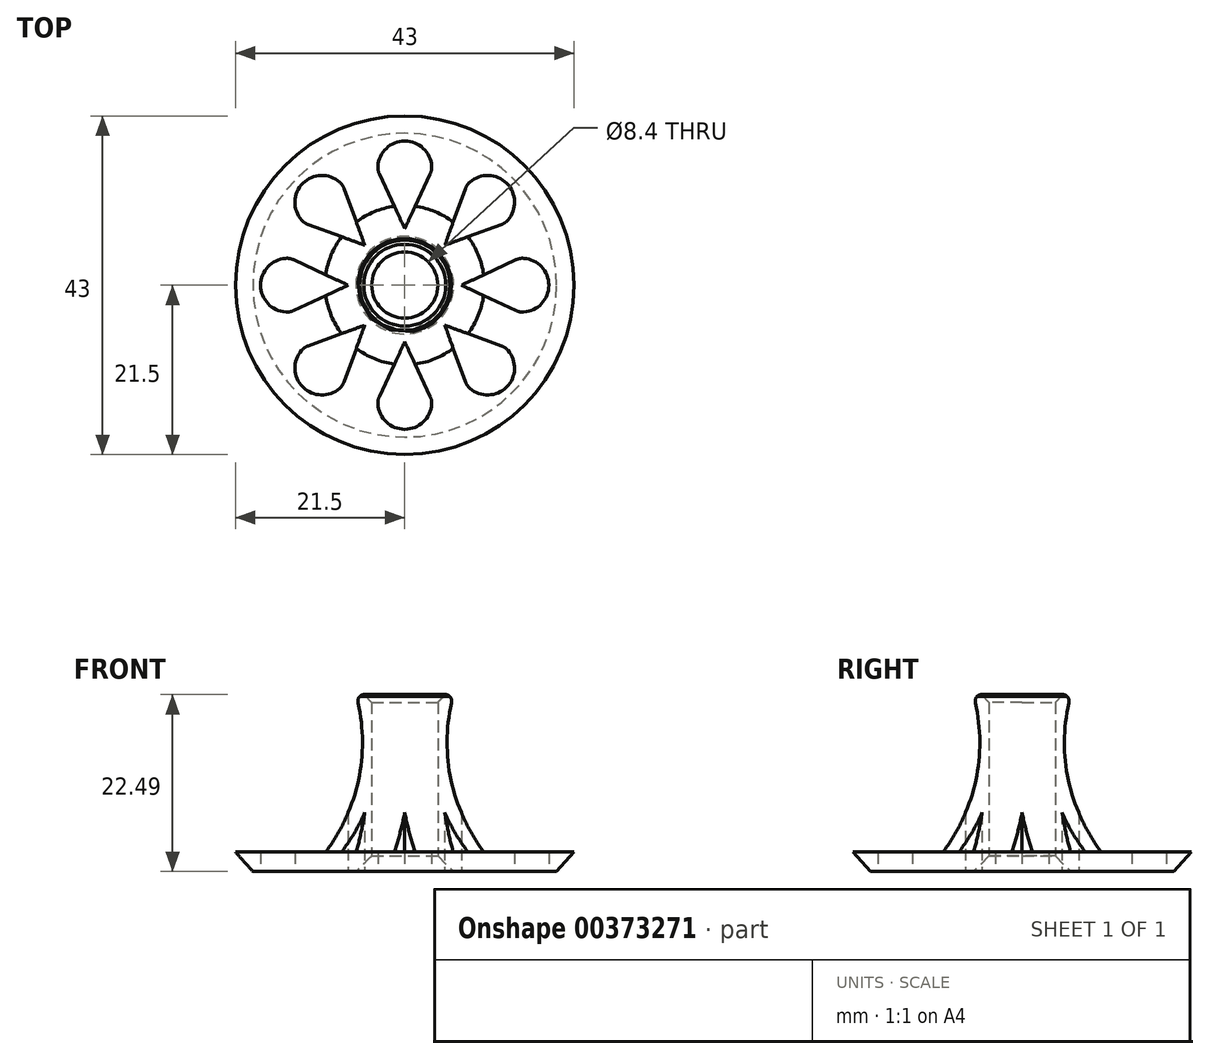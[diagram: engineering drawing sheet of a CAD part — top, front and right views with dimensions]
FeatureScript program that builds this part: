
annotation { "Feature Type Name" : "Feature", "Feature Type Description" : "" }
export const myFeature = defineFeature(function(context is Context, id is Id, definition is map)
    precondition{}
    {
        {
            var Q0;
            Q0=qCreatedBy(makeId("Front.planeOp"),FACE);
            var sketch = newSketch(context, id + "F0", { "sketchPlane" : qUnion([Q0])});
            skLineSegment(sketch, "E0", {"start": v(0, 0) * mm, "end": v(0, 0) * mm});
            skLineSegment(sketch, "E1", {"start": v(4.2, 0) * mm, "end": v(4.2, 22.5) * mm});
            skLineSegment(sketch, "E2", {"start": v(10.1, 2.5) * mm, "end": v(20.5, 2.5) * mm});
            skPoint(sketch, "E3.orphan", {"position": v(4.2, 2.5) * mm});
            skLineSegment(sketch, "E4", {"start": v(0, 0) * mm, "end": v(0, 23.46) * mm, "construction": true});
            skLineSegment(sketch, "E5.trimOffspring", {"start": v(4.2, 0) * mm, "end": v(19.3, 0) * mm});
            skArc(sketch, "E6", {"start": v(6.05, 21.87) * mm, "mid": v(5.86, 11.72) * mm, "end": v(10.1, 2.5) * mm});
            skLineSegment(sketch, "E7", {"start": v(5.53, 22.5) * mm, "end": v(6.05, 21.87) * mm});
            skPoint(sketch, "E8.orphan", {"position": v(7.2, 2.5) * mm});
            skLineSegment(sketch, "E9", {"start": v(4.2, 22.5) * mm, "end": v(5.53, 22.5) * mm});
            skLineSegment(sketch, "E10", {"start": v(20.5, 2.5) * mm, "end": v(21.5, 2.5) * mm});
            skLineSegment(sketch, "E11", {"start": v(19.3, 0) * mm, "end": v(21.5, 2.5) * mm});
            skSolve(sketch);
        }
        {
            var Q0;
            Q0 = qSketchRegion(id + "F0", true);
            var Q1;
            Q1=sQuery(id+"F0.wireOp",EDGE,"E4");
            revolve(context, id + "F1", {"entities" : qUnion([Q0]), "axis" : qUnion([Q1]), "revolveType" : RevolveType.FULL});
        }
        {
            var Q0;
            Q0=makeQuery(id+"F1.opRevolve","SWEPT_EDGE",EDGE,{"disambiguationData":[OSD([sQuery(id+"F0.wireOp",EDGE,"E1"),sQuery(id+"F0.wireOp",EDGE,"E5.trimOffspring")])]});
            chamfer(context, id + "F2", {"entities" : qUnion([Q0]), "width" : 2 * mm, "tangentPropagation" : true});
        }
        {
            var Q0;
            Q0=makeQuery(id+"F1.opRevolve","SWEPT_FACE",FACE,{"disambiguationData":[OSD([sQuery(id+"F0.wireOp",EDGE,"E5.trimOffspring")])]});
            var sketch = newSketch(context, id + "F3", { "sketchPlane" : qUnion([Q0])});
            skCircle(sketch, "E12.0", {"center": v(0, 0) * mm, "radius": 19.3 * mm});
            skCircle(sketch, "E12.1", {"center": v(0, 0) * mm, "radius": 6.2 * mm});
            skLineSegment(sketch, "E13", {"start": v(0, 19.3) * mm, "end": v(0, 0) * mm, "construction": true});
            skLineSegment(sketch, "E14", {"start": v(0, 0) * mm, "end": v(-19.3, 0) * mm, "construction": true});
            skCircle(sketch, "E15", {"center": v(0, 0) * mm, "radius": 14.88 * mm, "construction": true});
            skArc(sketch, "E16", {"start": v(3.41, 15.1) * mm, "mid": v(0, 18.3) * mm, "end": v(-3.41, 15.1) * mm});
            skLineSegment(sketch, "E17", {"start": v(3.23, 14.13) * mm, "end": v(0, 7.19) * mm});
            skLineSegment(sketch, "E18.MirrorCS", {"start": v(-3.23, 14.13) * mm, "end": v(0, 7.19) * mm});
            skPoint(sketch, "E19.visualSharp", {"position": v(-3.4, 14.5) * mm});
            skArc(sketch, "E19.filletArc", {"start": v(-3.41, 15.1) * mm, "mid": v(-3.38, 14.6) * mm, "end": v(-3.23, 14.13) * mm});
            skPoint(sketch, "E20.visualSharp", {"position": v(3.4, 14.5) * mm});
            skArc(sketch, "E20.filletArc", {"start": v(3.23, 14.13) * mm, "mid": v(3.38, 14.6) * mm, "end": v(3.41, 15.1) * mm});
            skArc(sketch, "E21.1.0", {"start": v(-8.27, 13.1) * mm, "mid": v(-12.94, 12.94) * mm, "end": v(-13.1, 8.27) * mm});
            skLineSegment(sketch, "E21.1.1", {"start": v(-12.28, 7.7) * mm, "end": v(-5.08, 5.08) * mm});
            skLineSegment(sketch, "E21.1.2", {"start": v(-7.7, 12.28) * mm, "end": v(-5.08, 5.08) * mm});
            skArc(sketch, "E21.1.3", {"start": v(-7.7, 12.28) * mm, "mid": v(-7.94, 12.72) * mm, "end": v(-8.27, 13.1) * mm});
            skArc(sketch, "E21.1.4", {"start": v(-13.1, 8.27) * mm, "mid": v(-12.72, 7.94) * mm, "end": v(-12.28, 7.7) * mm});
            skArc(sketch, "E21.2.0", {"start": v(-15.1, 3.41) * mm, "mid": v(-18.3, 0) * mm, "end": v(-15.1, -3.41) * mm});
            skLineSegment(sketch, "E21.2.1", {"start": v(-14.13, -3.23) * mm, "end": v(-7.19, 0) * mm});
            skLineSegment(sketch, "E21.2.2", {"start": v(-14.13, 3.23) * mm, "end": v(-7.19, 0) * mm});
            skArc(sketch, "E21.2.3", {"start": v(-14.13, 3.23) * mm, "mid": v(-14.6, 3.38) * mm, "end": v(-15.1, 3.41) * mm});
            skArc(sketch, "E21.2.4", {"start": v(-15.1, -3.41) * mm, "mid": v(-14.6, -3.38) * mm, "end": v(-14.13, -3.23) * mm});
            skArc(sketch, "E21.3.0", {"start": v(-13.1, -8.27) * mm, "mid": v(-12.94, -12.94) * mm, "end": v(-8.27, -13.1) * mm});
            skLineSegment(sketch, "E21.3.1", {"start": v(-7.7, -12.28) * mm, "end": v(-5.08, -5.08) * mm});
            skLineSegment(sketch, "E21.3.2", {"start": v(-12.28, -7.7) * mm, "end": v(-5.08, -5.08) * mm});
            skArc(sketch, "E21.3.3", {"start": v(-12.28, -7.7) * mm, "mid": v(-12.72, -7.94) * mm, "end": v(-13.1, -8.27) * mm});
            skArc(sketch, "E21.3.4", {"start": v(-8.27, -13.1) * mm, "mid": v(-7.94, -12.72) * mm, "end": v(-7.7, -12.28) * mm});
            skArc(sketch, "E21.4.0", {"start": v(-3.41, -15.1) * mm, "mid": v(0, -18.3) * mm, "end": v(3.41, -15.1) * mm});
            skLineSegment(sketch, "E21.4.1", {"start": v(3.23, -14.13) * mm, "end": v(0, -7.19) * mm});
            skLineSegment(sketch, "E21.4.2", {"start": v(-3.23, -14.13) * mm, "end": v(0, -7.19) * mm});
            skArc(sketch, "E21.4.3", {"start": v(-3.23, -14.13) * mm, "mid": v(-3.38, -14.6) * mm, "end": v(-3.41, -15.1) * mm});
            skArc(sketch, "E21.4.4", {"start": v(3.41, -15.1) * mm, "mid": v(3.38, -14.6) * mm, "end": v(3.23, -14.13) * mm});
            skArc(sketch, "E21.5.0", {"start": v(8.27, -13.1) * mm, "mid": v(12.94, -12.94) * mm, "end": v(13.1, -8.27) * mm});
            skLineSegment(sketch, "E21.5.1", {"start": v(12.28, -7.7) * mm, "end": v(5.08, -5.08) * mm});
            skLineSegment(sketch, "E21.5.2", {"start": v(7.7, -12.28) * mm, "end": v(5.08, -5.08) * mm});
            skArc(sketch, "E21.5.3", {"start": v(7.7, -12.28) * mm, "mid": v(7.94, -12.72) * mm, "end": v(8.27, -13.1) * mm});
            skArc(sketch, "E21.5.4", {"start": v(13.1, -8.27) * mm, "mid": v(12.72, -7.94) * mm, "end": v(12.28, -7.7) * mm});
            skArc(sketch, "E21.6.0", {"start": v(15.1, -3.41) * mm, "mid": v(18.3, 0) * mm, "end": v(15.1, 3.41) * mm});
            skLineSegment(sketch, "E21.6.1", {"start": v(14.13, 3.23) * mm, "end": v(7.19, 0) * mm});
            skLineSegment(sketch, "E21.6.2", {"start": v(14.13, -3.23) * mm, "end": v(7.19, 0) * mm});
            skArc(sketch, "E21.6.3", {"start": v(14.13, -3.23) * mm, "mid": v(14.6, -3.38) * mm, "end": v(15.1, -3.41) * mm});
            skArc(sketch, "E21.6.4", {"start": v(15.1, 3.41) * mm, "mid": v(14.6, 3.38) * mm, "end": v(14.13, 3.23) * mm});
            skArc(sketch, "E21.7.0", {"start": v(13.1, 8.27) * mm, "mid": v(12.94, 12.94) * mm, "end": v(8.27, 13.1) * mm});
            skLineSegment(sketch, "E21.7.1", {"start": v(7.7, 12.28) * mm, "end": v(5.08, 5.08) * mm});
            skLineSegment(sketch, "E21.7.2", {"start": v(12.28, 7.7) * mm, "end": v(5.08, 5.08) * mm});
            skArc(sketch, "E21.7.3", {"start": v(12.28, 7.7) * mm, "mid": v(12.72, 7.94) * mm, "end": v(13.1, 8.27) * mm});
            skArc(sketch, "E21.7.4", {"start": v(8.27, 13.1) * mm, "mid": v(7.94, 12.72) * mm, "end": v(7.7, 12.28) * mm});
            skSolve(sketch);
        }
        {
            var Q0;
            Q0=makeQuery(id+"F3.imprint","IMPRINT",FACE,{"disambiguationData":[TD([[makeQuery(id+"F3.imprint","IMPRINT",EDGE,{"derivedFrom":sQuery(id+"F3.wireOp",EDGE,"E21.6.0")}),1.0]])]});
            var Q1;
            Q1=makeQuery(id+"F3.imprint","IMPRINT",FACE,{"disambiguationData":[TD([[makeQuery(id+"F3.imprint","IMPRINT",EDGE,{"derivedFrom":sQuery(id+"F3.wireOp",EDGE,"E21.7.0")}),1.0]])]});
            var Q2;
            Q2=makeQuery(id+"F3.imprint","IMPRINT",FACE,{"disambiguationData":[TD([[makeQuery(id+"F3.imprint","IMPRINT",EDGE,{"derivedFrom":sQuery(id+"F3.wireOp",EDGE,"E16")}),1.0]])]});
            var Q3;
            Q3=makeQuery(id+"F3.imprint","IMPRINT",FACE,{"disambiguationData":[TD([[makeQuery(id+"F3.imprint","IMPRINT",EDGE,{"derivedFrom":sQuery(id+"F3.wireOp",EDGE,"E21.1.0")}),1.0]])]});
            var Q4;
            Q4=makeQuery(id+"F3.imprint","IMPRINT",FACE,{"disambiguationData":[TD([[makeQuery(id+"F3.imprint","IMPRINT",EDGE,{"derivedFrom":sQuery(id+"F3.wireOp",EDGE,"E21.2.0")}),1.0]])]});
            var Q5;
            Q5=makeQuery(id+"F3.imprint","IMPRINT",FACE,{"disambiguationData":[TD([[makeQuery(id+"F3.imprint","IMPRINT",EDGE,{"derivedFrom":sQuery(id+"F3.wireOp",EDGE,"E21.3.0")}),1.0]])]});
            var Q6;
            Q6=makeQuery(id+"F3.imprint","IMPRINT",FACE,{"disambiguationData":[TD([[makeQuery(id+"F3.imprint","IMPRINT",EDGE,{"derivedFrom":sQuery(id+"F3.wireOp",EDGE,"E21.4.0")}),1.0]])]});
            var Q7;
            Q7=makeQuery(id+"F3.imprint","IMPRINT",FACE,{"disambiguationData":[TD([[makeQuery(id+"F3.imprint","IMPRINT",EDGE,{"derivedFrom":sQuery(id+"F3.wireOp",EDGE,"E21.5.0")}),1.0]])]});
            extrude(context, id + "F4", {"entities" : qUnion([Q0, Q1, Q2, Q3, Q4, Q5, Q6, Q7]), "operationType" : NewBodyOperationType.REMOVE, "oppositeDirection" : true, "depth" : 25 * mm});
        }
        {
            var Q0;
            Q0=makeQuery(id+"F1.opRevolve","SWEPT_EDGE",EDGE,{"disambiguationData":[OSD([sQuery(id+"F0.wireOp",EDGE,"E6"),sQuery(id+"F0.wireOp",EDGE,"E7")])]});
            fillet(context, id + "F5", {"entities" : qUnion([Q0]), "radius" : 1 * mm, "tangentPropagation" : true, "allowEdgeOverflow" : false});
        }
        {
            var Q0;
            Q0=makeQuery(id+"F1.opRevolve","SWEPT_EDGE",EDGE,{"disambiguationData":[OSD([sQuery(id+"F0.wireOp",EDGE,"E7"),sQuery(id+"F0.wireOp",EDGE,"E9")])]});
            fillet(context, id + "F6", {"entities" : qUnion([Q0]), "radius" : 1 * mm, "tangentPropagation" : true, "allowEdgeOverflow" : false});
        }
        {
            var Q0;
            Q0=makeQuery(id+"F1.opRevolve","SWEPT_EDGE",EDGE,{"disambiguationData":[OSD([sQuery(id+"F0.wireOp",EDGE,"E1"),sQuery(id+"F0.wireOp",EDGE,"E9")])]});
            chamfer(context, id + "F7", {"entities" : qUnion([Q0]), "width" : 1 * mm, "tangentPropagation" : true});
        }
    });
